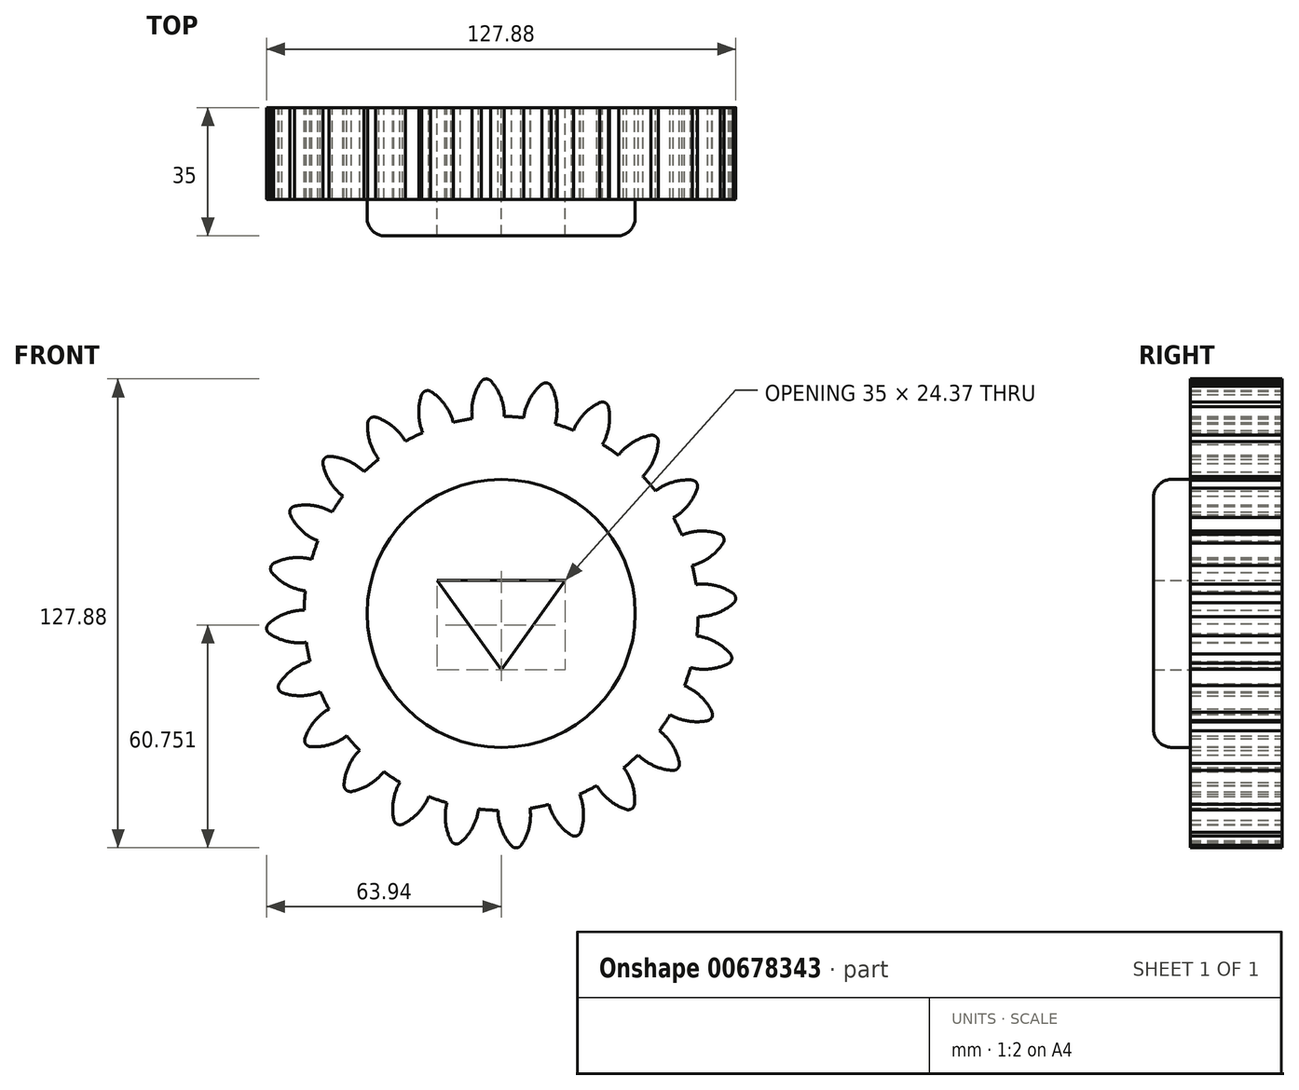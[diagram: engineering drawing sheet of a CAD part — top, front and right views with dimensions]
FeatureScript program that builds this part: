
annotation { "Feature Type Name" : "Feature", "Feature Type Description" : "" }
export const myFeature = defineFeature(function(context is Context, id is Id, definition is map)
    precondition{}
    {
        {
            var Q0;
            Q0=qCreatedBy(makeId("Front.planeOp"),FACE);
            var sketch = newSketch(context, id + "F0", { "sketchPlane" : qUnion([Q0])});
            skCircle(sketch, "E0", {"center": v(0, 0) * mm, "radius": 53.72 * mm});
            skCircle(sketch, "E1", {"center": v(0, 0) * mm, "radius": 58.67 * mm, "construction": true});
            skCircle(sketch, "E2", {"center": v(0, 0) * mm, "radius": 63.5 * mm, "construction": true});
            skLineSegment(sketch, "E3", {"start": v(0, 0) * mm, "end": v(0, 72.86) * mm, "construction": true});
            skLineSegment(sketch, "E4", {"start": v(0, 0) * mm, "end": v(-5.98, 91.23) * mm, "construction": true});
            skLineSegment(sketch, "E5", {"start": v(0, 58.67) * mm, "end": v(-61.73, 58.67) * mm, "construction": true});
            skLineSegment(sketch, "E6", {"start": v(0, 58.67) * mm, "end": v(-58, 37.57) * mm, "construction": true});
            skCircle(sketch, "E7", {"center": v(0, 0) * mm, "radius": 55.14 * mm, "construction": true});
            skCircle(sketch, "E8", {"center": v(0, 58.67) * mm, "radius": 14.6 * mm, "construction": true});
            skCircle(sketch, "E9", {"center": v(-13.72, 53.68) * mm, "radius": 14.6 * mm, "construction": true});
            skArc(sketch, "E10", {"start": v(0, 58.67) * mm, "mid": v(-1.2, 61.2) * mm, "end": v(-2.86, 63.44) * mm});
            skArc(sketch, "E11", {"start": v(0.88, 53.71) * mm, "mid": v(0.66, 56.23) * mm, "end": v(0, 58.67) * mm});
            skArc(sketch, "E12.MirrorCS", {"start": v(-7.66, 58.17) * mm, "mid": v(-6.8, 60.83) * mm, "end": v(-5.45, 63.27) * mm});
            skArc(sketch, "E13.MirrorCS", {"start": v(-7.88, 53.14) * mm, "mid": v(-8, 55.67) * mm, "end": v(-7.66, 58.17) * mm});
            skArc(sketch, "E14", {"start": v(-2.86, 63.44) * mm, "mid": v(-4.2, 63.94) * mm, "end": v(-5.45, 63.27) * mm});
            skCircle(sketch, "E15", {"center": v(0, 0) * mm, "radius": 36.56 * mm});
            skLineSegment(sketch, "E16", {"start": v(-17.5, 9) * mm, "end": v(17.5, 9) * mm});
            skLineSegment(sketch, "E17", {"start": v(17.5, 9) * mm, "end": v(0, -15.37) * mm});
            skLineSegment(sketch, "E18", {"start": v(0, -15.37) * mm, "end": v(-17.5, 9) * mm});
            skSolve(sketch);
        }
        {
            var Q0;
            Q0 = qSketchRegion(id + "F0", true);
            extrude(context, id + "F1", {"entities" : qUnion([Q0]), "depth" : 25 * mm, "offsetDistance" : 25 * mm});
        }
        {
            var Q0;
            Q0=makeQuery(id+"F1.opExtrude","SWEPT_BODY",BODY,{"disambiguationData":[OSD([sQuery(id+"F0.wireOp",EDGE,"E0"),sQuery(id+"F0.wireOp",EDGE,"E10"),sQuery(id+"F0.wireOp",EDGE,"E11"),sQuery(id+"F0.wireOp",EDGE,"E12.MirrorCS"),sQuery(id+"F0.wireOp",EDGE,"E13.MirrorCS"),sQuery(id+"F0.wireOp",EDGE,"E14"),sQuery(id+"F0.wireOp",EDGE,"E15")])]});
            var Q1;
            Q1=makeQuery(id+"F1.opExtrude","SWEPT_FACE",FACE,{"disambiguationData":[OSD([sQuery(id+"F0.wireOp",EDGE,"E0")])]});
            circularPattern(context, id + "F2", {"entities" : qUnion([Q0]), "axis" : qUnion([Q1]), "angle" : 360 * degree, "instanceCount" : 24, "equalSpace" : true});
        }
        {
            var Q0;
            Q0=makeQuery(id+"F0.imprint","IMPRINT",FACE,{"disambiguationData":[TD([[makeQuery(id+"F0.imprint","IMPRINT",EDGE,{"derivedFrom":sQuery(id+"F0.wireOp",EDGE,"E15")}),1.0]])]});
            extrude(context, id + "F3", {"entities" : qUnion([Q0]), "operationType" : NewBodyOperationType.ADD, "depth" : 35 * mm, "offsetDistance" : 25 * mm});
        }
        {
            var Q0;
            Q0=makeQuery(id+"F3.opExtrude","CAP_EDGE",EDGE,{"disambiguationData":[OSD([sQuery(id+"F0.wireOp",EDGE,"E15")])],"isStart":false});
            fillet(context, id + "F4", {"entities" : qUnion([Q0]), "radius" : 5 * mm, "tangentPropagation" : true, "allowEdgeOverflow" : false});
        }
    });
